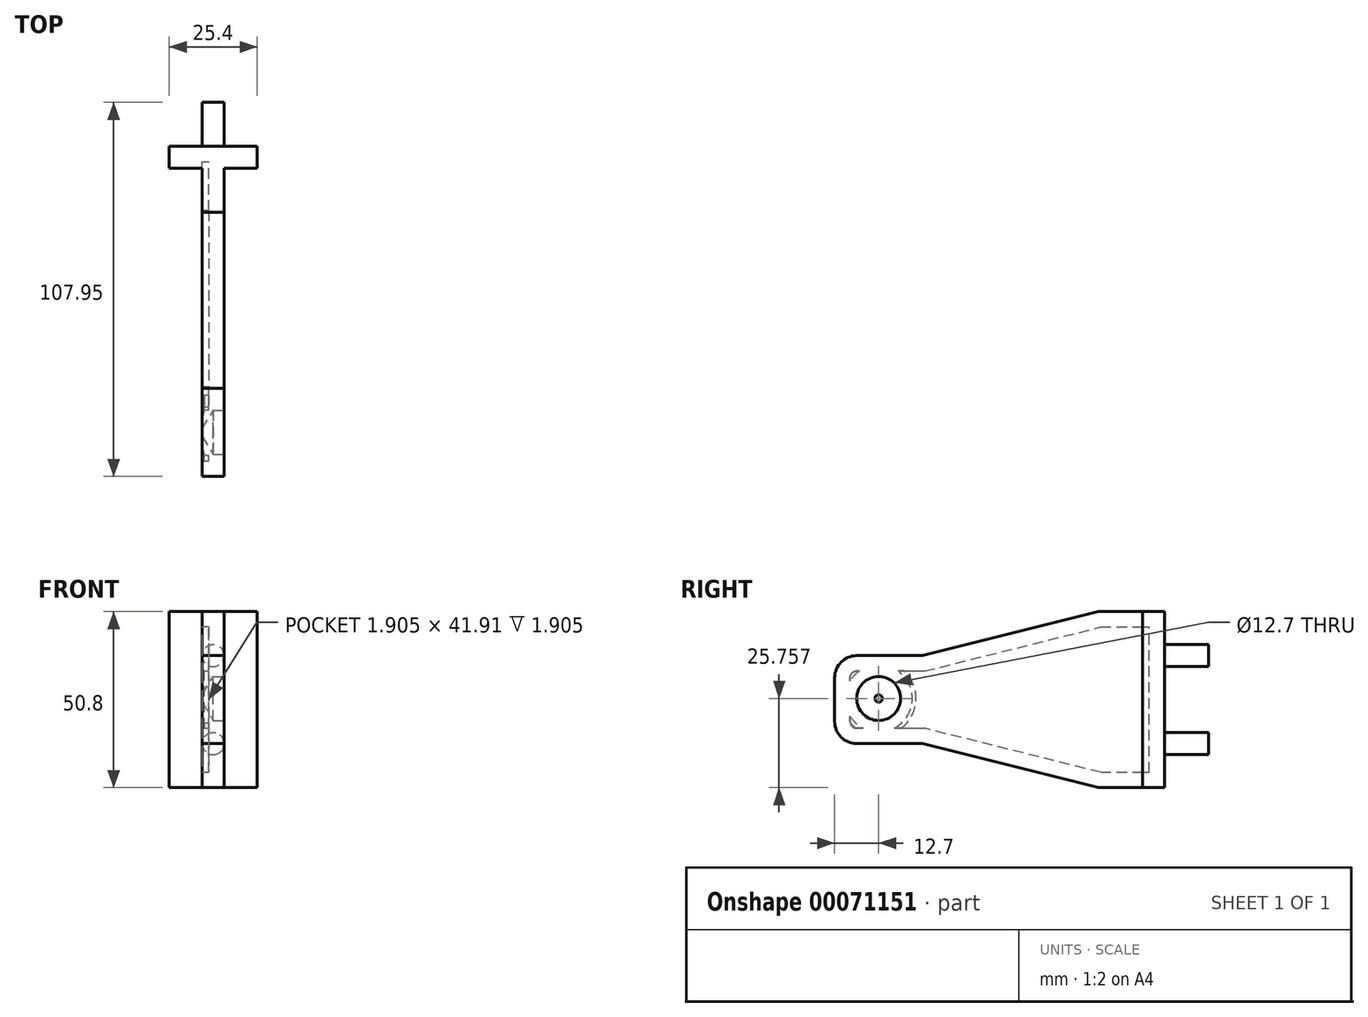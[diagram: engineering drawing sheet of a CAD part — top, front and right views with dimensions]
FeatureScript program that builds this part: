
annotation { "Feature Type Name" : "Feature", "Feature Type Description" : "" }
export const myFeature = defineFeature(function(context is Context, id is Id, definition is map)
    precondition{}
    {
        {
            var Q0;
            Q0=qCreatedBy(makeId("Front.planeOp"),FACE);
            var sketch = newSketch(context, id + "F0", { "sketchPlane" : qUnion([Q0])});
            skLineSegment(sketch, "E0.bottom", {"start": v(-11.47, 22.44) * mm, "end": v(13.93, 22.44) * mm});
            skLineSegment(sketch, "E0.top", {"start": v(-11.47, -28.36) * mm, "end": v(13.93, -28.36) * mm});
            skLineSegment(sketch, "E0.left", {"start": v(-11.47, 22.44) * mm, "end": v(-11.47, -28.36) * mm});
            skLineSegment(sketch, "E0.right", {"start": v(13.93, 22.44) * mm, "end": v(13.93, -28.36) * mm});
            skSolve(sketch);
        }
        {
            var Q0;
            Q0=makeQuery(id+"F0.imprint","IMPRINT",FACE,{"disambiguationData":[TD([[makeQuery(id+"F0.imprint","IMPRINT",EDGE,{"derivedFrom":sQuery(id+"F0.wireOp",EDGE,"E0.bottom")}),-1.0]])]});
            extrude(context, id + "F1", {"entities" : qUnion([Q0]), "depth" : 6.35 * mm});
        }
        {
            var Q0;
            Q0=makeQuery(id+"F1.opExtrude","CAP_FACE",FACE,{"disambiguationData":[OSD([sQuery(id+"F0.wireOp",EDGE,"E0.bottom"),sQuery(id+"F0.wireOp",EDGE,"E0.top"),sQuery(id+"F0.wireOp",EDGE,"E0.left"),sQuery(id+"F0.wireOp",EDGE,"E0.right")])],"isStart":false});
            var sketch = newSketch(context, id + "F2", { "sketchPlane" : qUnion([Q0])});
            skLineSegment(sketch, "E1.bottom", {"start": v(-1.94, 22.44) * mm, "end": v(4.4, 22.44) * mm});
            skLineSegment(sketch, "E1.top", {"start": v(-1.94, -28.36) * mm, "end": v(4.4, -28.36) * mm});
            skLineSegment(sketch, "E1.left", {"start": v(-1.94, 22.44) * mm, "end": v(-1.94, -28.36) * mm});
            skLineSegment(sketch, "E1.right", {"start": v(4.4, 22.44) * mm, "end": v(4.4, -28.36) * mm});
            skSolve(sketch);
        }
        {
            var Q0;
            Q0=makeQuery(id+"F2.imprint","IMPRINT",FACE,{"disambiguationData":[TD([[makeQuery(id+"F2.imprint","IMPRINT",EDGE,{"derivedFrom":sQuery(id+"F2.wireOp",EDGE,"E1.bottom")}),-1.0]])]});
            extrude(context, id + "F3", {"entities" : qUnion([Q0]), "operationType" : NewBodyOperationType.ADD, "depth" : 12.7 * mm});
        }
        {
            var Q0;
            Q0=makeQuery(id+"F3.opExtrude","CAP_FACE",FACE,{"disambiguationData":[OSD([sQuery(id+"F2.wireOp",EDGE,"E1.bottom"),sQuery(id+"F2.wireOp",EDGE,"E1.top"),sQuery(id+"F2.wireOp",EDGE,"E1.left"),sQuery(id+"F2.wireOp",EDGE,"E1.right")])],"isStart":false});
            cPlane(context, id + "F4", {"entities" : qUnion([Q0]), "cplaneType" : CPlaneType.OFFSET, "offset" : 50.8 * mm, "width" : 152.4 * mm, "height" : 152.4 * mm});
        }
        {
            var Q0;
            Q0=qCreatedBy(id+"F4.planeOp",FACE);
            var sketch = newSketch(context, id + "F5", { "sketchPlane" : qUnion([Q0])});
            skLineSegment(sketch, "E2.0", {"start": v(-1.94, 9.74) * mm, "end": v(-1.94, -15.66) * mm});
            skLineSegment(sketch, "E3.0", {"start": v(4.4, 9.74) * mm, "end": v(4.4, -15.66) * mm});
            skLineSegment(sketch, "E4", {"start": v(-1.94, 9.74) * mm, "end": v(4.4, 9.74) * mm});
            skLineSegment(sketch, "E5", {"start": v(-1.94, -15.66) * mm, "end": v(4.4, -15.66) * mm});
            skSolve(sketch);
        }
        {
            var Q1;
            Q1=makeQuery(id+"F3.opExtrude","CAP_FACE",FACE,{"disambiguationData":[OSD([sQuery(id+"F2.wireOp",EDGE,"E1.bottom"),sQuery(id+"F2.wireOp",EDGE,"E1.top"),sQuery(id+"F2.wireOp",EDGE,"E1.left"),sQuery(id+"F2.wireOp",EDGE,"E1.right")])],"isStart":false});
            var Q2;
            Q2=makeQuery(id+"F5.imprint","IMPRINT",FACE,{"disambiguationData":[TD([[makeQuery(id+"F5.imprint","IMPRINT",EDGE,{"derivedFrom":sQuery(id+"F5.wireOp",EDGE,"E2.0")}),1.0]])]});
            loft(context, id + "F6", {"operationType" : NewBodyOperationType.ADD, "sheetProfilesArray" : [{ "sheetProfileEntities" : qUnion([Q1]) }, { "sheetProfileEntities" : qUnion([Q2]) }]});
        }
        {
            var Q0;
            Q0=makeQuery(id+"F6.opLoft","CAP_FACE",FACE,{"disambiguationData":[OSD([makeQuery(id+"F5.imprint","IMPRINT",FACE,{"disambiguationData":[TD([[makeQuery(id+"F5.imprint","IMPRINT",EDGE,{"derivedFrom":sQuery(id+"F5.wireOp",EDGE,"E2.0")}),1.0]])]})])],"isStart":true});
            extrude(context, id + "F7", {"entities" : qUnion([Q0]), "operationType" : NewBodyOperationType.ADD, "depth" : 25.4 * mm});
        }
        {
            var Q0;
            Q0=makeQuery(id+"F7.opExtrude","CAP_EDGE",EDGE,{"disambiguationData":[OSD([sQuery(id+"F5.wireOp",EDGE,"E2.0"),sQuery(id+"F5.wireOp",EDGE,"E3.0"),sQuery(id+"F5.wireOp",EDGE,"E4")])],"isStart":false});
            var Q1;
            Q1=makeQuery(id+"F7.opExtrude","CAP_EDGE",EDGE,{"disambiguationData":[OSD([sQuery(id+"F5.wireOp",EDGE,"E2.0"),sQuery(id+"F5.wireOp",EDGE,"E3.0"),sQuery(id+"F5.wireOp",EDGE,"E5")])],"isStart":false});
            fillet(context, id + "F8", {"entities" : qUnion([Q0, Q1]), "radius" : 6.35 * mm, "tangentPropagation" : true, "allowEdgeOverflow" : false});
        }
        {
            var Q0;
            {var subQ0=sQuery(id+"F5.wireOp",EDGE,"E5");var subQ1=sQuery(id+"F5.wireOp",EDGE,"E4");var subQ2=sQuery(id+"F5.wireOp",EDGE,"E3.0");var subQ3=sQuery(id+"F2.wireOp",EDGE,"E1.right");Q0=makeQuery(id+"F7.boolean.opBoolean","MERGE",FACE,{"derivedFrom":[makeQuery(id+"F6.boolean.opBoolean","MERGE",FACE,{"derivedFrom":[makeQuery(id+"F3.opExtrude","SWEPT_FACE",FACE,{"disambiguationData":[OSD([subQ3])]}),makeQuery(id+"F6.opLoft","SWEPT_FACE",FACE,{"disambiguationData":[OSD([sQuery(id+"F0.wireOp",EDGE,"E0.bottom"),sQuery(id+"F0.wireOp",EDGE,"E0.top"),sQuery(id+"F2.wireOp",EDGE,"E1.bottom"),sQuery(id+"F2.wireOp",EDGE,"E1.top"),subQ3,subQ2,subQ1,subQ0])]})]}),makeQuery(id+"F7.opExtrude","SWEPT_FACE",FACE,{"disambiguationData":[OSD([subQ2,subQ1,subQ0])]})]});}
            var sketch = newSketch(context, id + "F9", { "sketchPlane" : qUnion([Q0])});
            skPoint(sketch, "E6", {"position": v(-82.55, -2.6) * mm});
            skPoint(sketch, "E7", {"position": v(-95.25, -2.6) * mm});
            skSolve(sketch);
        }
        {
            var Q0;
            Q0=sQuery(id+"F9.wireOp",VERTEX,"E6");
            var Q1;
            Q1=makeQuery(id+"F1.opExtrude","SWEPT_BODY",BODY,{"disambiguationData":[OSD([sQuery(id+"F0.wireOp",EDGE,"E0.bottom"),sQuery(id+"F0.wireOp",EDGE,"E0.top"),sQuery(id+"F0.wireOp",EDGE,"E0.left"),sQuery(id+"F0.wireOp",EDGE,"E0.right")])]});
            hole(context, id + "F10", {"style" : HoleStyle.SIMPLE, "holeDiameter" : 12.7 * mm, "endStyle" : HoleEndStyle.BLIND, "holeDepth" : 3.17 * mm, "locations" : qUnion([Q0]), "scope" : qUnion([Q1])});
        }
        {
            var Q0;
            Q0=makeQuery(id+"F1.opExtrude","CAP_FACE",FACE,{"disambiguationData":[OSD([sQuery(id+"F0.wireOp",EDGE,"E0.bottom"),sQuery(id+"F0.wireOp",EDGE,"E0.top"),sQuery(id+"F0.wireOp",EDGE,"E0.left"),sQuery(id+"F0.wireOp",EDGE,"E0.right")])],"isStart":true});
            var sketch = newSketch(context, id + "F11", { "sketchPlane" : qUnion([Q0])});
            skPoint(sketch, "E8", {"position": v(-1.23, -28.36) * mm});
            skPoint(sketch, "E9", {"position": v(-1.23, 22.44) * mm});
            skCircle(sketch, "E10", {"center": v(-1.23, 9.74) * mm, "radius": 3.18 * mm});
            skCircle(sketch, "E11", {"center": v(-1.23, -15.66) * mm, "radius": 3.18 * mm});
            skSolve(sketch);
        }
        {
            var Q0;
            Q0=makeQuery(id+"F11.imprint","IMPRINT",FACE,{"disambiguationData":[TD([[makeQuery(id+"F11.imprint","IMPRINT",EDGE,{"derivedFrom":sQuery(id+"F11.wireOp",EDGE,"E10")}),1.0]])]});
            var Q1;
            Q1=makeQuery(id+"F11.imprint","IMPRINT",FACE,{"disambiguationData":[TD([[makeQuery(id+"F11.imprint","IMPRINT",EDGE,{"derivedFrom":sQuery(id+"F11.wireOp",EDGE,"E11")}),1.0]])]});
            extrude(context, id + "F12", {"entities" : qUnion([Q0, Q1]), "operationType" : NewBodyOperationType.ADD, "depth" : 12.7 * mm});
        }
        {
            var Q0;
            {var subQ0=sQuery(id+"F5.wireOp",EDGE,"E5");var subQ1=sQuery(id+"F5.wireOp",EDGE,"E4");var subQ2=sQuery(id+"F5.wireOp",EDGE,"E2.0");var subQ3=sQuery(id+"F2.wireOp",EDGE,"E1.left");Q0=makeQuery(id+"F7.boolean.opBoolean","MERGE",FACE,{"derivedFrom":[makeQuery(id+"F6.boolean.opBoolean","MERGE",FACE,{"derivedFrom":[makeQuery(id+"F3.opExtrude","SWEPT_FACE",FACE,{"disambiguationData":[OSD([subQ3])]}),makeQuery(id+"F6.opLoft","SWEPT_FACE",FACE,{"disambiguationData":[OSD([sQuery(id+"F0.wireOp",EDGE,"E0.bottom"),sQuery(id+"F0.wireOp",EDGE,"E0.top"),sQuery(id+"F2.wireOp",EDGE,"E1.bottom"),sQuery(id+"F2.wireOp",EDGE,"E1.top"),subQ3,subQ2,subQ1,subQ0])]})]}),makeQuery(id+"F7.opExtrude","SWEPT_FACE",FACE,{"disambiguationData":[OSD([subQ2,subQ1,subQ0])]})]});}
            shell(context, id + "F13", {"entities" : qUnion([Q0]), "thickness" : 4.44 * mm});
        }
    });
